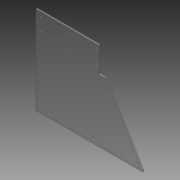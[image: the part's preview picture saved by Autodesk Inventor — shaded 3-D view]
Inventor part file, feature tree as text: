
AUTODESK INVENTOR PART (.ipt)
format: ipt  version: 2014 SP1 (Build 180222100, 222)  size: 96,768 bytes
history: native  units: in
note: dims shown in document units (in); Inventor stores cm internally (conversion verified against a paired STEP export)
features: extrude x1, sketch x1, reference x1
ambient origin geometry x8: Origin, YZ Plane, XZ Plane, XY Plane, X Axis, Y Axis, Z Axis, Center Point
bodies: Solid1 (feature_tree)
feature tree (3):
  extrude  "Extrusion1"  Depth=0.125in
  sketch  "Sketch1"  dims[d0=7.0in d1=8.5in d2=5.0in d3=2.0in d5=0.125in d6=0.0in d7=0.125in d8=1.1811in d10=2.25in d11=0.7874in d13=1.0in d16=0.375in d17=0.375in d18=0.5in]
  reference  "Reference1"
